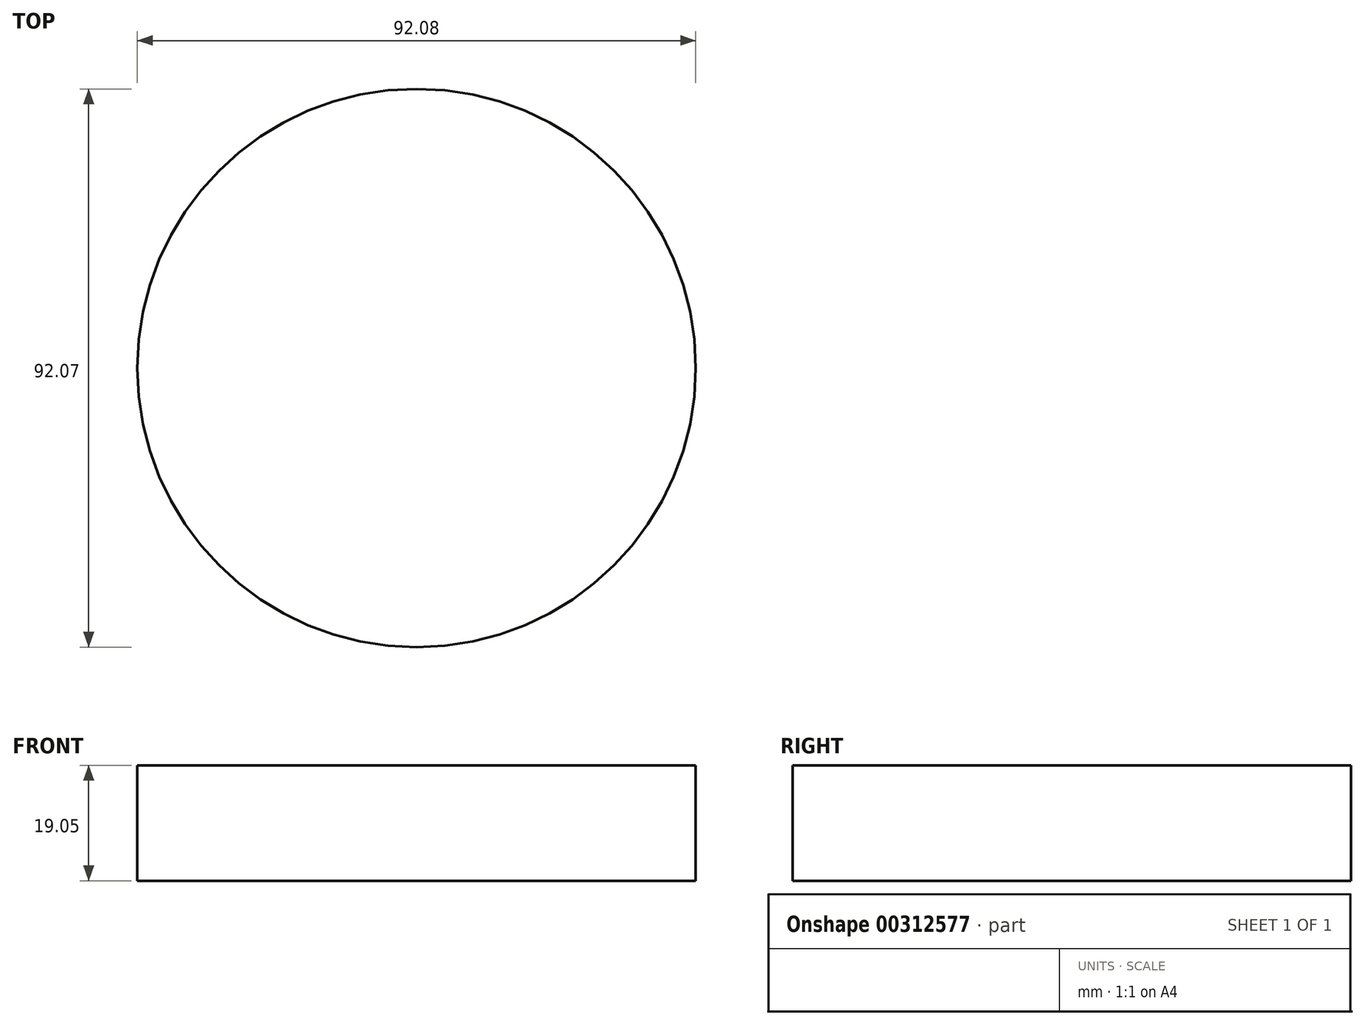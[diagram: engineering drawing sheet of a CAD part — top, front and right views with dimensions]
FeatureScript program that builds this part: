
annotation { "Feature Type Name" : "Feature", "Feature Type Description" : "" }
export const myFeature = defineFeature(function(context is Context, id is Id, definition is map)
    precondition{}
    {
        {
            var Q0;
            Q0=qCreatedBy(makeId("Top.planeOp"),FACE);
            var sketch = newSketch(context, id + "F0", { "sketchPlane" : qUnion([Q0])});
            skLineSegment(sketch, "E0", {"start": v(145.58, -278.48) * mm, "end": v(-159.22, -278.48) * mm});
            skLineSegment(sketch, "E1", {"start": v(-159.22, -278.48) * mm, "end": v(-159.22, -532.48) * mm});
            skLineSegment(sketch, "E2", {"start": v(-159.22, -532.48) * mm, "end": v(145.58, -532.48) * mm});
            skLineSegment(sketch, "E3", {"start": v(145.58, -278.48) * mm, "end": v(145.58, -532.48) * mm});
            skLineSegment(sketch, "E4", {"start": v(145.58, -11.78) * mm, "end": v(145.58, -265.78) * mm});
            skLineSegment(sketch, "E5", {"start": v(-159.22, -265.78) * mm, "end": v(145.58, -265.78) * mm});
            skLineSegment(sketch, "E6", {"start": v(-159.22, -11.78) * mm, "end": v(-159.22, -265.78) * mm});
            skLineSegment(sketch, "E7", {"start": v(145.58, -11.78) * mm, "end": v(-159.22, -11.78) * mm});
            skLineSegment(sketch, "E8", {"start": v(145.58, 254.92) * mm, "end": v(145.58, 0.92) * mm});
            skLineSegment(sketch, "E9", {"start": v(-159.22, 0.92) * mm, "end": v(145.58, 0.92) * mm});
            skLineSegment(sketch, "E10", {"start": v(-159.22, 254.92) * mm, "end": v(-159.22, 0.92) * mm});
            skLineSegment(sketch, "E11", {"start": v(145.58, 254.92) * mm, "end": v(-159.22, 254.92) * mm});
            skLineSegment(sketch, "E12", {"start": v(-79.36, -351.24) * mm, "end": v(32.78, -335.67) * mm});
            skArc(sketch, "E13", {"start": v(32.78, -335.67) * mm, "mid": v(112.96, -405.48) * mm, "end": v(32.78, -475.3) * mm});
            skLineSegment(sketch, "E14", {"start": v(32.78, -475.3) * mm, "end": v(-79.36, -459.73) * mm});
            skArc(sketch, "E15", {"start": v(-79.36, -459.73) * mm, "mid": v(-126.6, -405.48) * mm, "end": v(-79.36, -351.24) * mm});
            skArc(sketch, "E16", {"start": v(-75.87, -434.57) * mm, "mid": v(-101.2, -405.48) * mm, "end": v(-75.87, -376.4) * mm});
            skLineSegment(sketch, "E17", {"start": v(-75.87, -376.4) * mm, "end": v(-7.58, -366.91) * mm});
            skArc(sketch, "E18", {"start": v(-7.58, -366.91) * mm, "mid": v(-4.42, -368.41) * mm, "end": v(-4.56, -371.9) * mm});
            skArc(sketch, "E19", {"start": v(-4.56, -371.9) * mm, "mid": v(-15.31, -405.48) * mm, "end": v(-4.56, -439.06) * mm});
            skArc(sketch, "E20", {"start": v(-4.56, -439.06) * mm, "mid": v(-4.42, -442.55) * mm, "end": v(-7.58, -444.05) * mm});
            skLineSegment(sketch, "E21", {"start": v(-7.58, -444.05) * mm, "end": v(-75.87, -434.57) * mm});
            skArc(sketch, "E22", {"start": v(-36.82, 333.52) * mm, "mid": v(-66.33, 359.53) * mm, "end": v(-77.3, 397.3) * mm});
            skArc(sketch, "E23", {"start": v(-77.3, 397.3) * mm, "mid": v(-73.32, 420.67) * mm, "end": v(-61.81, 441.4) * mm});
            skArc(sketch, "E24", {"start": v(-61.81, 441.4) * mm, "mid": v(-58.7, 447) * mm, "end": v(-57.62, 453.32) * mm});
            skLineSegment(sketch, "E25", {"start": v(-57.62, 453.32) * mm, "end": v(-57.62, 486.2) * mm});
            skLineSegment(sketch, "E26", {"start": v(-57.62, 486.2) * mm, "end": v(43.98, 486.2) * mm});
            skLineSegment(sketch, "E27", {"start": v(43.98, 486.2) * mm, "end": v(43.98, 453.32) * mm});
            skArc(sketch, "E28", {"start": v(43.98, 453.32) * mm, "mid": v(45.06, 447) * mm, "end": v(48.17, 441.4) * mm});
            skArc(sketch, "E29", {"start": v(48.17, 441.4) * mm, "mid": v(59.68, 420.67) * mm, "end": v(63.66, 397.3) * mm});
            skArc(sketch, "E30", {"start": v(63.66, 397.3) * mm, "mid": v(52.69, 359.53) * mm, "end": v(23.17, 333.52) * mm});
            skArc(sketch, "E31", {"start": v(23.17, 333.52) * mm, "mid": v(15.2, 326.49) * mm, "end": v(12.23, 316.28) * mm});
            skLineSegment(sketch, "E32", {"start": v(12.23, 316.28) * mm, "end": v(12.23, 302.05) * mm});
            skArc(sketch, "E33", {"start": v(12.23, 302.05) * mm, "mid": v(10.37, 297.56) * mm, "end": v(5.88, 295.7) * mm});
            skLineSegment(sketch, "E34", {"start": v(5.88, 295.7) * mm, "end": v(-3.65, 295.7) * mm});
            skLineSegment(sketch, "E35", {"start": v(-3.65, 295.7) * mm, "end": v(-3.65, 352.33) * mm});
            skArc(sketch, "E36", {"start": v(-3.65, 352.33) * mm, "mid": v(7.85, 354.67) * mm, "end": v(18.36, 359.9) * mm});
            skArc(sketch, "E37", {"start": v(18.36, 359.9) * mm, "mid": v(20.05, 360.44) * mm, "end": v(21.77, 359.99) * mm});
            skArc(sketch, "E38", {"start": v(21.77, 359.99) * mm, "mid": v(29.55, 360.93) * mm, "end": v(30.5, 368.7) * mm});
            skArc(sketch, "E39", {"start": v(30.5, 368.7) * mm, "mid": v(30.04, 370.43) * mm, "end": v(30.58, 372.12) * mm});
            skArc(sketch, "E40", {"start": v(30.58, 372.12) * mm, "mid": v(38.26, 397.3) * mm, "end": v(30.58, 422.48) * mm});
            skArc(sketch, "E41", {"start": v(30.58, 422.48) * mm, "mid": v(30.04, 424.18) * mm, "end": v(30.5, 425.9) * mm});
            skArc(sketch, "E42", {"start": v(30.5, 425.9) * mm, "mid": v(29.55, 433.67) * mm, "end": v(21.77, 434.62) * mm});
            skArc(sketch, "E43", {"start": v(21.77, 434.62) * mm, "mid": v(20.05, 434.16) * mm, "end": v(18.36, 434.7) * mm});
            skArc(sketch, "E44", {"start": v(18.36, 434.7) * mm, "mid": v(-6.82, 442.39) * mm, "end": v(-32, 434.7) * mm});
            skArc(sketch, "E45", {"start": v(-32, 434.7) * mm, "mid": v(-33.7, 434.16) * mm, "end": v(-35.42, 434.62) * mm});
            skArc(sketch, "E46", {"start": v(-35.42, 434.62) * mm, "mid": v(-43.2, 433.67) * mm, "end": v(-44.14, 425.9) * mm});
            skArc(sketch, "E47", {"start": v(-44.14, 425.9) * mm, "mid": v(-43.68, 424.18) * mm, "end": v(-44.22, 422.48) * mm});
            skArc(sketch, "E48", {"start": v(-44.22, 422.48) * mm, "mid": v(-51.9, 397.3) * mm, "end": v(-44.22, 372.12) * mm});
            skArc(sketch, "E49", {"start": v(-44.22, 372.12) * mm, "mid": v(-43.68, 370.43) * mm, "end": v(-44.14, 368.7) * mm});
            skArc(sketch, "E50", {"start": v(-44.14, 368.7) * mm, "mid": v(-43.2, 360.93) * mm, "end": v(-35.42, 359.99) * mm});
            skArc(sketch, "E51", {"start": v(-35.42, 359.99) * mm, "mid": v(-33.7, 360.44) * mm, "end": v(-32, 359.9) * mm});
            skArc(sketch, "E52", {"start": v(-32, 359.9) * mm, "mid": v(-21.5, 354.67) * mm, "end": v(-10, 352.33) * mm});
            skLineSegment(sketch, "E53", {"start": v(-10, 352.33) * mm, "end": v(-10, 295.7) * mm});
            skLineSegment(sketch, "E54", {"start": v(-10, 295.7) * mm, "end": v(-19.52, 295.7) * mm});
            skArc(sketch, "E55", {"start": v(-19.52, 295.7) * mm, "mid": v(-24.01, 297.56) * mm, "end": v(-25.87, 302.05) * mm});
            skLineSegment(sketch, "E56", {"start": v(-25.87, 302.05) * mm, "end": v(-25.87, 316.28) * mm});
            skArc(sketch, "E57", {"start": v(-25.87, 316.28) * mm, "mid": v(-28.84, 326.49) * mm, "end": v(-36.82, 333.52) * mm});
            skLineSegment(sketch, "E58", {"start": v(-46.03, -68.97) * mm, "end": v(66.11, -84.54) * mm});
            skArc(sketch, "E59", {"start": v(66.11, -84.54) * mm, "mid": v(113.35, -138.78) * mm, "end": v(66.11, -193.03) * mm});
            skLineSegment(sketch, "E60", {"start": v(66.11, -193.03) * mm, "end": v(-46.03, -208.6) * mm});
            skArc(sketch, "E61", {"start": v(-46.03, -208.6) * mm, "mid": v(-126.2, -138.78) * mm, "end": v(-46.03, -68.97) * mm});
            skArc(sketch, "E62", {"start": v(63.42, -365.56) * mm, "mid": v(57.7, -359.41) * mm, "end": v(57.06, -351.03) * mm});
            skLineSegment(sketch, "E63", {"start": v(57.06, -351.03) * mm, "end": v(60.71, -337.4) * mm});
            skArc(sketch, "E64", {"start": v(60.71, -337.4) * mm, "mid": v(46.83, -335.13) * mm, "end": v(32.78, -335.67) * mm});
            skLineSegment(sketch, "E65", {"start": v(32.78, -335.67) * mm, "end": v(24.09, -336.87) * mm});
            skLineSegment(sketch, "E66", {"start": v(24.09, -336.87) * mm, "end": v(27.88, -351.03) * mm});
            skArc(sketch, "E67", {"start": v(27.88, -351.03) * mm, "mid": v(27.25, -359.41) * mm, "end": v(21.52, -365.56) * mm});
            skArc(sketch, "E68", {"start": v(21.52, -365.56) * mm, "mid": v(42.47, -450.57) * mm, "end": v(63.42, -365.56) * mm});
            skCircle(sketch, "E69", {"center": v(58.58, -138.78) * mm, "radius": 29.37 * mm});
            skCircle(sketch, "E70", {"center": v(42.47, -405.48) * mm, "radius": 19.05 * mm});
            skCircle(sketch, "E71", {"center": v(88.33, -109.04) * mm, "radius": 9.53 * mm});
            skCircle(sketch, "E72", {"center": v(8.3, -89.33) * mm, "radius": 9.53 * mm});
            skCircle(sketch, "E73", {"center": v(8.3, -188.24) * mm, "radius": 9.53 * mm});
            skCircle(sketch, "E74", {"center": v(-96.58, -97.92) * mm, "radius": 9.53 * mm});
            skCircle(sketch, "E75", {"center": v(-55.72, -138.78) * mm, "radius": 46.04 * mm});
            skCircle(sketch, "E76", {"center": v(88.33, -168.53) * mm, "radius": 9.53 * mm});
            skCircle(sketch, "E77", {"center": v(-96.58, -179.64) * mm, "radius": 9.53 * mm});
            skCircle(sketch, "E78", {"center": v(82.94, -364.62) * mm, "radius": 9.53 * mm});
            skCircle(sketch, "E79", {"center": v(-21.94, -356.03) * mm, "radius": 9.53 * mm});
            skCircle(sketch, "E80", {"center": v(-101.97, -375.74) * mm, "radius": 9.53 * mm});
            skCircle(sketch, "E81", {"center": v(-101.97, -435.23) * mm, "radius": 9.53 * mm});
            skCircle(sketch, "E82", {"center": v(-21.94, -454.94) * mm, "radius": 9.53 * mm});
            skCircle(sketch, "E83", {"center": v(82.94, -446.34) * mm, "radius": 9.53 * mm});
            skCircle(sketch, "E84", {"center": v(50.96, 397.3) * mm, "radius": 4.76 * mm});
            skCircle(sketch, "E85", {"center": v(-64.6, 397.3) * mm, "radius": 4.76 * mm});
            skCircle(sketch, "E86", {"center": v(71.36, -355.44) * mm, "radius": 4.76 * mm});
            skCircle(sketch, "E87", {"center": v(13.58, -455.53) * mm, "radius": 4.76 * mm});
            skCircle(sketch, "E88", {"center": v(13.58, -355.44) * mm, "radius": 4.76 * mm});
            skCircle(sketch, "E89", {"center": v(71.36, -455.53) * mm, "radius": 4.76 * mm});
            skCircle(sketch, "E90", {"center": v(-6.82, 127.92) * mm, "radius": 46.04 * mm});
            skCircle(sketch, "E91", {"center": v(-35.71, 77.87) * mm, "radius": 4.76 * mm});
            skCircle(sketch, "E92", {"center": v(22.07, 177.96) * mm, "radius": 4.76 * mm});
            skCircle(sketch, "E93", {"center": v(22.07, 77.87) * mm, "radius": 4.76 * mm});
            skCircle(sketch, "E94", {"center": v(-35.71, 177.96) * mm, "radius": 4.76 * mm});
            skCircle(sketch, "E95", {"center": v(-6.82, 127.92) * mm, "radius": 70.48 * mm});
            skCircle(sketch, "E96", {"center": v(-26.83, -88.74) * mm, "radius": 3.18 * mm});
            skCircle(sketch, "E97", {"center": v(-84.61, -88.74) * mm, "radius": 3.18 * mm});
            skCircle(sketch, "E98", {"center": v(-84.61, -188.83) * mm, "radius": 3.18 * mm});
            skCircle(sketch, "E99", {"center": v(-26.83, -188.83) * mm, "radius": 3.18 * mm});
            skSolve(sketch);
        }
        {
            var Q0;
            Q0=makeQuery(id+"F0.imprint","IMPRINT",FACE,{"disambiguationData":[TD([[makeQuery(id+"F0.imprint","IMPRINT",EDGE,{"derivedFrom":sQuery(id+"F0.wireOp",EDGE,"E90")}),1.0]])]});
            extrude(context, id + "F1", {"entities" : qUnion([Q0]), "oppositeDirection" : true, "depth" : 19.05 * mm});
        }
    });
